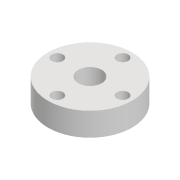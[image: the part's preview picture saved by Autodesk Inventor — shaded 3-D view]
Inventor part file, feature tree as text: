
AUTODESK INVENTOR PART (.ipt)
format: ipt  version: 2022 (Build 260153000, 153)  size: 103,936 bytes
history: native  units: mm
features: extrude x1, sketch x1
ambient origin geometry x8: Origin, YZ Plane, XZ Plane, XY Plane, X Axis, Y Axis, Z Axis, Center Point
bodies: Solid1 (feature_tree)
feature tree (2):
  extrude  "Extrusion1"  Depth=5.0mm
  sketch  "Sketch1"  dims[d0=18.0mm d1=5.0mm d2=2.4mm d3=7.0mm d4=40.0mm d6=360.0deg d8=5.0mm d9=0.0mm]
